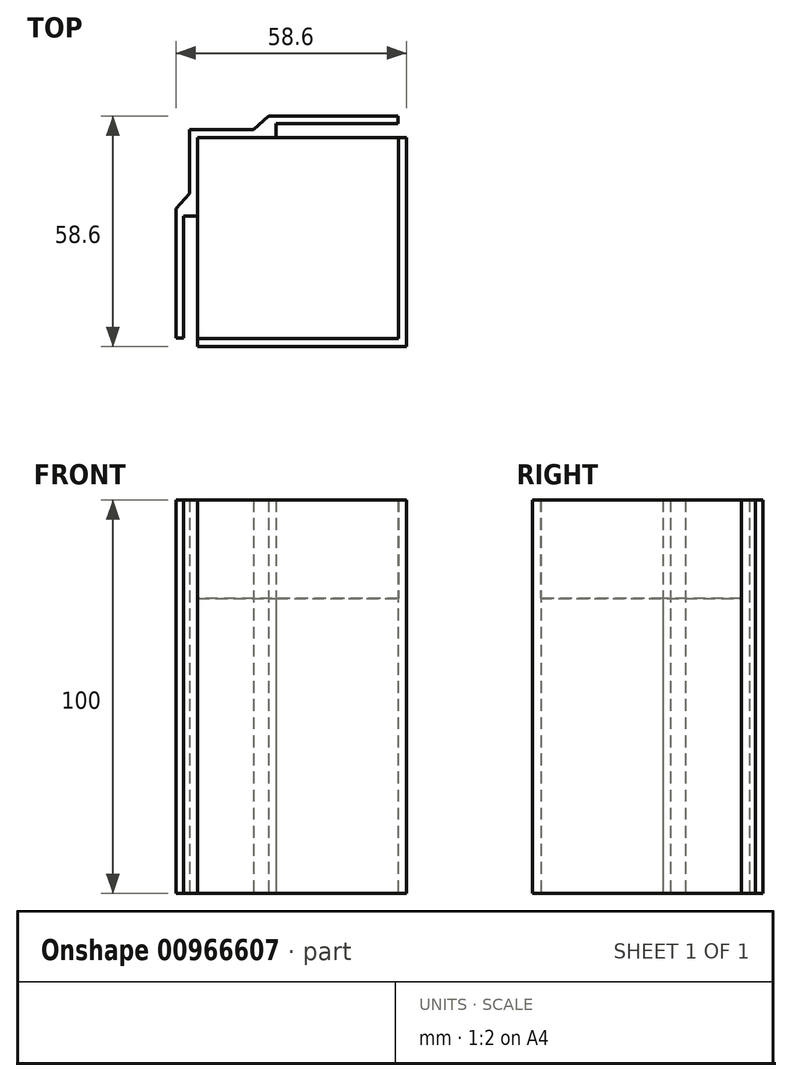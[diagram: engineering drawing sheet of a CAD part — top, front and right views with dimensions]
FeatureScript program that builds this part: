
annotation { "Feature Type Name" : "Feature", "Feature Type Description" : "" }
export const myFeature = defineFeature(function(context is Context, id is Id, definition is map)
    precondition{}
    {
        {
            var Q0;
            Q0=qCreatedBy(makeId("Top.planeOp"),FACE);
            var sketch = newSketch(context, id + "F0", { "sketchPlane" : qUnion([Q0])});
            skLineSegment(sketch, "E0.bottom", {"start": v(-25.5, 25.52) * mm, "end": v(25.5, 25.52) * mm});
            skLineSegment(sketch, "E0.top", {"start": v(-25.5, -25.48) * mm, "end": v(25.5, -25.48) * mm});
            skLineSegment(sketch, "E0.left", {"start": v(-25.5, 25.52) * mm, "end": v(-25.5, -25.48) * mm});
            skLineSegment(sketch, "E0.right", {"start": v(25.5, 25.52) * mm, "end": v(25.5, -25.48) * mm});
            skLineSegment(sketch, "E1", {"start": v(-25.5, 0.02) * mm, "end": v(25.5, 0.02) * mm});
            skLineSegment(sketch, "E2", {"start": v(0, 25.52) * mm, "end": v(0, -25.48) * mm});
            skLineSegment(sketch, "E3", {"start": v(-25.5, 25.52) * mm, "end": v(-25.5, 5.52) * mm});
            skLineSegment(sketch, "E4", {"start": v(-25.5, 5.52) * mm, "end": v(-29, 5.52) * mm});
            skLineSegment(sketch, "E5", {"start": v(-25.5, -25.48) * mm, "end": v(-29, -25.48) * mm});
            skLineSegment(sketch, "E6", {"start": v(-29, 5.52) * mm, "end": v(-29, -25.48) * mm});
            skLineSegment(sketch, "E7.0", {"start": v(-31, 7.52) * mm, "end": v(-31, -25.48) * mm});
            skLineSegment(sketch, "E7.1", {"start": v(-25.5, 7.52) * mm, "end": v(-31, 7.52) * mm});
            skLineSegment(sketch, "E8", {"start": v(-31, -25.48) * mm, "end": v(-29, -25.48) * mm});
            skLineSegment(sketch, "E9", {"start": v(-25.5, 25.52) * mm, "end": v(-5.5, 25.52) * mm});
            skLineSegment(sketch, "E10", {"start": v(-5.5, 25.52) * mm, "end": v(-5.5, 29.02) * mm});
            skLineSegment(sketch, "E11", {"start": v(25.5, 25.52) * mm, "end": v(25.5, 29.02) * mm});
            skLineSegment(sketch, "E12", {"start": v(-5.5, 29.02) * mm, "end": v(25.5, 29.02) * mm});
            skLineSegment(sketch, "E13.0", {"start": v(-7.5, 31.02) * mm, "end": v(25.5, 31.02) * mm});
            skLineSegment(sketch, "E13.1", {"start": v(-7.5, 25.52) * mm, "end": v(-7.5, 31.02) * mm});
            skLineSegment(sketch, "E14", {"start": v(25.5, 31.02) * mm, "end": v(25.5, 29.02) * mm});
            skLineSegment(sketch, "E15", {"start": v(-7.5, 25.52) * mm, "end": v(-7.56, 25.52) * mm});
            skLineSegment(sketch, "E16", {"start": v(-7.56, 25.52) * mm, "end": v(-7.5, 31.02) * mm});
            skLineSegment(sketch, "E17", {"start": v(-25.5, 7.52) * mm, "end": v(-25.5, 7.53) * mm});
            skLineSegment(sketch, "E18", {"start": v(-25.5, 7.53) * mm, "end": v(-31, 7.52) * mm});
            skLineSegment(sketch, "E19.0", {"start": v(-27.5, 27.52) * mm, "end": v(-0.5, 27.52) * mm});
            skLineSegment(sketch, "E19.1", {"start": v(-27.5, 27.52) * mm, "end": v(-27.5, 0.52) * mm});
            skLineSegment(sketch, "E20.0", {"start": v(-25.5, -25.58) * mm, "end": v(25.6, -25.58) * mm});
            skLineSegment(sketch, "E20.1", {"start": v(25.6, 25.52) * mm, "end": v(25.6, -25.58) * mm});
            skLineSegment(sketch, "E21.0", {"start": v(27.6, 25.52) * mm, "end": v(27.6, -27.58) * mm});
            skLineSegment(sketch, "E21.1", {"start": v(-25.5, -27.58) * mm, "end": v(27.6, -27.58) * mm});
            skLineSegment(sketch, "E22", {"start": v(-25.5, -25.48) * mm, "end": v(-25.5, -27.58) * mm});
            skLineSegment(sketch, "E23", {"start": v(27.6, 25.52) * mm, "end": v(25.5, 25.52) * mm});
            skLineSegment(sketch, "E24", {"start": v(-7.5, 31.02) * mm, "end": v(-13.36, 25.52) * mm});
            skLineSegment(sketch, "E25", {"start": v(-31, 7.52) * mm, "end": v(-25.5, 13.45) * mm});
            skSolve(sketch);
        }
        {
            var Q0;
            {var subQ0=sQuery(id+"F0.wireOp",EDGE,"E0.right");var subQ1=sQuery(id+"F0.wireOp",EDGE,"E0.top");var subQ2=makeQuery(id+"F0.imprint","INTERSECT",VERTEX,{"derivedFrom":[subQ1,subQ0]});Q0=makeQuery(id+"F0.imprint","IMPRINT",FACE,{"disambiguationData":[TD([[makeQuery(id+"F0.imprint","IMPRINT",EDGE,{"disambiguationData":[TD([[subQ2,1.0]])],"derivedFrom":subQ1}),1.0]])]});}
            var Q1;
            {var subQ6=sQuery(id+"F0.wireOp",EDGE,"E0.bottom");var subQ11=makeQuery(id+"F0.imprint","INTERSECT",VERTEX,{"derivedFrom":[subQ6,sQuery(id+"F0.wireOp",EDGE,"E24")]});Q1=makeQuery(id+"F0.imprint","IMPRINT",FACE,{"disambiguationData":[TD([[makeQuery(id+"F0.imprint","IMPRINT",EDGE,{"disambiguationData":[TD([[subQ11,1.0]])],"derivedFrom":subQ6}),-1.0]])]});}
            var Q2;
            {var subQ0=sQuery(id+"F0.wireOp",EDGE,"E7.1");var subQ1=sQuery(id+"F0.wireOp",EDGE,"E0.left");var subQ2=makeQuery(id+"F0.imprint","INTERSECT",VERTEX,{"derivedFrom":[subQ1,subQ0]});Q2=makeQuery(id+"F0.imprint","IMPRINT",FACE,{"disambiguationData":[TD([[makeQuery(id+"F0.imprint","IMPRINT",EDGE,{"disambiguationData":[TD([[subQ2,-1.0]])],"derivedFrom":subQ1}),-1.0]])]});}
            var Q3;
            {var subQ0=sQuery(id+"F0.wireOp",EDGE,"E13.1");var subQ1=sQuery(id+"F0.wireOp",EDGE,"E0.bottom");var subQ2=makeQuery(id+"F0.imprint","INTERSECT",VERTEX,{"derivedFrom":[subQ1,subQ0]});Q3=makeQuery(id+"F0.imprint","IMPRINT",FACE,{"disambiguationData":[TD([[makeQuery(id+"F0.imprint","IMPRINT",EDGE,{"disambiguationData":[TD([[subQ2,-1.0]])],"derivedFrom":subQ1}),1.0]])]});}
            var Q4;
            {var subQ3=sQuery(id+"F0.wireOp",EDGE,"E20.0");Q4=makeQuery(id+"F0.imprint","IMPRINT",FACE,{"disambiguationData":[TD([[makeQuery(id+"F0.imprint","IMPRINT",EDGE,{"derivedFrom":subQ3}),-1.0]])]});}
            var Q5;
            {var subQ1=sQuery(id+"F0.wireOp",EDGE,"E7.1");var subQ3=sQuery(id+"F0.wireOp",EDGE,"E19.1");var subQ4=makeQuery(id+"F0.imprint","INTERSECT",VERTEX,{"derivedFrom":[subQ1,subQ3]});Q5=makeQuery(id+"F0.imprint","IMPRINT",FACE,{"disambiguationData":[TD([[makeQuery(id+"F0.imprint","IMPRINT",EDGE,{"disambiguationData":[TD([[subQ4,1.0]])],"derivedFrom":subQ3}),-1.0]])]});}
            var Q6;
            {var subQ1=sQuery(id+"F0.wireOp",EDGE,"E13.1");var subQ3=sQuery(id+"F0.wireOp",EDGE,"E19.0");var subQ4=makeQuery(id+"F0.imprint","INTERSECT",VERTEX,{"derivedFrom":[subQ1,subQ3]});Q6=makeQuery(id+"F0.imprint","IMPRINT",FACE,{"disambiguationData":[TD([[makeQuery(id+"F0.imprint","IMPRINT",EDGE,{"disambiguationData":[TD([[subQ4,1.0]])],"derivedFrom":subQ3}),1.0]])]});}
            var Q7;
            {var subQ3=sQuery(id+"F0.wireOp",EDGE,"E24");var subQ9=sQuery(id+"F0.wireOp",EDGE,"E0.bottom");var subQ11=makeQuery(id+"F0.imprint","INTERSECT",VERTEX,{"derivedFrom":[subQ9,subQ3]});Q7=makeQuery(id+"F0.imprint","IMPRINT",FACE,{"disambiguationData":[TD([[makeQuery(id+"F0.imprint","IMPRINT",EDGE,{"disambiguationData":[TD([[subQ11,1.0]])],"derivedFrom":subQ9}),1.0]])]});}
            var Q8;
            {var subQ6=sQuery(id+"F0.wireOp",EDGE,"E6");Q8=makeQuery(id+"F0.imprint","IMPRINT",FACE,{"disambiguationData":[TD([[makeQuery(id+"F0.imprint","IMPRINT",EDGE,{"derivedFrom":subQ6}),-1.0]])]});}
            var Q9;
            {var subQ4=sQuery(id+"F0.wireOp",EDGE,"E12");Q9=makeQuery(id+"F0.imprint","IMPRINT",FACE,{"disambiguationData":[TD([[makeQuery(id+"F0.imprint","IMPRINT",EDGE,{"derivedFrom":subQ4}),1.0]])]});}
            var Q10;
            {var subQ0=sQuery(id+"F0.wireOp",EDGE,"E2");var subQ5=sQuery(id+"F0.wireOp",EDGE,"E1");var subQ7=makeQuery(id+"F0.imprint","INTERSECT",VERTEX,{"derivedFrom":[subQ5,subQ0]});Q10=makeQuery(id+"F0.imprint","IMPRINT",FACE,{"disambiguationData":[TD([[makeQuery(id+"F0.imprint","IMPRINT",EDGE,{"disambiguationData":[TD([[subQ7,-1.0]])],"derivedFrom":subQ5}),1.0]])]});}
            var Q11;
            {var subQ4=sQuery(id+"F0.wireOp",EDGE,"E20.0");Q11=makeQuery(id+"F0.imprint","IMPRINT",FACE,{"disambiguationData":[TD([[makeQuery(id+"F0.imprint","IMPRINT",EDGE,{"derivedFrom":subQ4}),1.0]])]});}
            var Q12;
            {var subQ0=sQuery(id+"F0.wireOp",EDGE,"E0.left");var subQ5=sQuery(id+"F0.wireOp",EDGE,"E1");var subQ6=makeQuery(id+"F0.imprint","INTERSECT",VERTEX,{"derivedFrom":[subQ0,subQ5]});Q12=makeQuery(id+"F0.imprint","IMPRINT",FACE,{"disambiguationData":[TD([[makeQuery(id+"F0.imprint","IMPRINT",EDGE,{"disambiguationData":[TD([[subQ6,-1.0]])],"derivedFrom":subQ5}),-1.0]])]});}
            var Q13;
            {var subQ0=sQuery(id+"F0.wireOp",EDGE,"E7.1");var subQ1=sQuery(id+"F0.wireOp",EDGE,"E0.left");var subQ2=makeQuery(id+"F0.imprint","INTERSECT",VERTEX,{"derivedFrom":[subQ1,subQ0]});Q13=makeQuery(id+"F0.imprint","IMPRINT",FACE,{"disambiguationData":[TD([[makeQuery(id+"F0.imprint","IMPRINT",EDGE,{"disambiguationData":[TD([[subQ2,1.0]])],"derivedFrom":subQ1}),-1.0]])]});}
            var Q14;
            {var subQ0=sQuery(id+"F0.wireOp",EDGE,"E13.1");var subQ1=sQuery(id+"F0.wireOp",EDGE,"E0.bottom");var subQ2=makeQuery(id+"F0.imprint","INTERSECT",VERTEX,{"derivedFrom":[subQ1,subQ0]});Q14=makeQuery(id+"F0.imprint","IMPRINT",FACE,{"disambiguationData":[TD([[makeQuery(id+"F0.imprint","IMPRINT",EDGE,{"disambiguationData":[TD([[subQ2,1.0]])],"derivedFrom":subQ1}),1.0]])]});}
            extrude(context, id + "F1", {"entities" : qUnion([Q0, Q1, Q2, Q3, Q4, Q5, Q6, Q7, Q8, Q9, Q10, Q11, Q12, Q13, Q14]), "depth" : 75 * mm, "offsetDistance" : 25 * mm});
        }
        {
            var Q0;
            {var subQ3=sQuery(id+"F0.wireOp",EDGE,"E24");var subQ9=sQuery(id+"F0.wireOp",EDGE,"E0.bottom");var subQ11=makeQuery(id+"F0.imprint","INTERSECT",VERTEX,{"derivedFrom":[subQ9,subQ3]});Q0=makeQuery(id+"F0.imprint","IMPRINT",FACE,{"disambiguationData":[TD([[makeQuery(id+"F0.imprint","IMPRINT",EDGE,{"disambiguationData":[TD([[subQ11,1.0]])],"derivedFrom":subQ9}),1.0]])]});}
            var Q1;
            {var subQ0=sQuery(id+"F0.wireOp",EDGE,"E13.1");var subQ1=sQuery(id+"F0.wireOp",EDGE,"E0.bottom");var subQ2=makeQuery(id+"F0.imprint","INTERSECT",VERTEX,{"derivedFrom":[subQ1,subQ0]});Q1=makeQuery(id+"F0.imprint","IMPRINT",FACE,{"disambiguationData":[TD([[makeQuery(id+"F0.imprint","IMPRINT",EDGE,{"disambiguationData":[TD([[subQ2,1.0]])],"derivedFrom":subQ1}),1.0]])]});}
            var Q2;
            {var subQ1=sQuery(id+"F0.wireOp",EDGE,"E13.1");var subQ3=sQuery(id+"F0.wireOp",EDGE,"E19.0");var subQ4=makeQuery(id+"F0.imprint","INTERSECT",VERTEX,{"derivedFrom":[subQ1,subQ3]});Q2=makeQuery(id+"F0.imprint","IMPRINT",FACE,{"disambiguationData":[TD([[makeQuery(id+"F0.imprint","IMPRINT",EDGE,{"disambiguationData":[TD([[subQ4,1.0]])],"derivedFrom":subQ3}),1.0]])]});}
            var Q3;
            {var subQ4=sQuery(id+"F0.wireOp",EDGE,"E12");Q3=makeQuery(id+"F0.imprint","IMPRINT",FACE,{"disambiguationData":[TD([[makeQuery(id+"F0.imprint","IMPRINT",EDGE,{"derivedFrom":subQ4}),1.0]])]});}
            var Q4;
            {var subQ0=sQuery(id+"F0.wireOp",EDGE,"E13.1");var subQ1=sQuery(id+"F0.wireOp",EDGE,"E0.bottom");var subQ2=makeQuery(id+"F0.imprint","INTERSECT",VERTEX,{"derivedFrom":[subQ1,subQ0]});Q4=makeQuery(id+"F0.imprint","IMPRINT",FACE,{"disambiguationData":[TD([[makeQuery(id+"F0.imprint","IMPRINT",EDGE,{"disambiguationData":[TD([[subQ2,-1.0]])],"derivedFrom":subQ1}),1.0]])]});}
            var Q5;
            {var subQ6=sQuery(id+"F0.wireOp",EDGE,"E6");Q5=makeQuery(id+"F0.imprint","IMPRINT",FACE,{"disambiguationData":[TD([[makeQuery(id+"F0.imprint","IMPRINT",EDGE,{"derivedFrom":subQ6}),-1.0]])]});}
            var Q6;
            {var subQ1=sQuery(id+"F0.wireOp",EDGE,"E7.1");var subQ3=sQuery(id+"F0.wireOp",EDGE,"E19.1");var subQ4=makeQuery(id+"F0.imprint","INTERSECT",VERTEX,{"derivedFrom":[subQ1,subQ3]});Q6=makeQuery(id+"F0.imprint","IMPRINT",FACE,{"disambiguationData":[TD([[makeQuery(id+"F0.imprint","IMPRINT",EDGE,{"disambiguationData":[TD([[subQ4,1.0]])],"derivedFrom":subQ3}),-1.0]])]});}
            var Q7;
            {var subQ0=sQuery(id+"F0.wireOp",EDGE,"E7.1");var subQ1=sQuery(id+"F0.wireOp",EDGE,"E0.left");var subQ2=makeQuery(id+"F0.imprint","INTERSECT",VERTEX,{"derivedFrom":[subQ1,subQ0]});Q7=makeQuery(id+"F0.imprint","IMPRINT",FACE,{"disambiguationData":[TD([[makeQuery(id+"F0.imprint","IMPRINT",EDGE,{"disambiguationData":[TD([[subQ2,1.0]])],"derivedFrom":subQ1}),-1.0]])]});}
            var Q8;
            {var subQ0=sQuery(id+"F0.wireOp",EDGE,"E7.1");var subQ1=sQuery(id+"F0.wireOp",EDGE,"E0.left");var subQ2=makeQuery(id+"F0.imprint","INTERSECT",VERTEX,{"derivedFrom":[subQ1,subQ0]});Q8=makeQuery(id+"F0.imprint","IMPRINT",FACE,{"disambiguationData":[TD([[makeQuery(id+"F0.imprint","IMPRINT",EDGE,{"disambiguationData":[TD([[subQ2,-1.0]])],"derivedFrom":subQ1}),-1.0]])]});}
            var Q9;
            {var subQ3=sQuery(id+"F0.wireOp",EDGE,"E20.0");Q9=makeQuery(id+"F0.imprint","IMPRINT",FACE,{"disambiguationData":[TD([[makeQuery(id+"F0.imprint","IMPRINT",EDGE,{"derivedFrom":subQ3}),-1.0]])]});}
            var Q10;
            {var subQ0=sQuery(id+"F0.wireOp",EDGE,"E25");var subQ1=sQuery(id+"F0.wireOp",EDGE,"E0.left");var subQ2=makeQuery(id+"F0.imprint","INTERSECT",VERTEX,{"derivedFrom":[subQ1,subQ0]});Q10=makeQuery(id+"F0.imprint","IMPRINT",FACE,{"disambiguationData":[TD([[makeQuery(id+"F0.imprint","IMPRINT",EDGE,{"disambiguationData":[TD([[subQ2,-1.0]])],"derivedFrom":subQ1}),-1.0]])]});}
            var Q11;
            {var subQ1=sQuery(id+"F0.wireOp",EDGE,"E18");var subQ3=sQuery(id+"F0.wireOp",EDGE,"E19.1");var subQ4=makeQuery(id+"F0.imprint","INTERSECT",VERTEX,{"derivedFrom":[subQ1,subQ3]});Q11=makeQuery(id+"F0.imprint","IMPRINT",FACE,{"disambiguationData":[TD([[makeQuery(id+"F0.imprint","IMPRINT",EDGE,{"disambiguationData":[TD([[subQ4,1.0]])],"derivedFrom":subQ3}),-1.0]])]});}
            var Q12;
            {var subQ1=sQuery(id+"F0.wireOp",EDGE,"E16");var subQ3=sQuery(id+"F0.wireOp",EDGE,"E19.0");var subQ4=makeQuery(id+"F0.imprint","INTERSECT",VERTEX,{"derivedFrom":[subQ1,subQ3]});Q12=makeQuery(id+"F0.imprint","IMPRINT",FACE,{"disambiguationData":[TD([[makeQuery(id+"F0.imprint","IMPRINT",EDGE,{"disambiguationData":[TD([[subQ4,1.0]])],"derivedFrom":subQ3}),1.0]])]});}
            var Q13;
            {var subQ0=sQuery(id+"F0.wireOp",EDGE,"E24");var subQ1=sQuery(id+"F0.wireOp",EDGE,"E0.bottom");var subQ2=makeQuery(id+"F0.imprint","INTERSECT",VERTEX,{"derivedFrom":[subQ1,subQ0]});Q13=makeQuery(id+"F0.imprint","IMPRINT",FACE,{"disambiguationData":[TD([[makeQuery(id+"F0.imprint","IMPRINT",EDGE,{"disambiguationData":[TD([[subQ2,-1.0]])],"derivedFrom":subQ1}),1.0]])]});}
            extrude(context, id + "F2", {"entities" : qUnion([Q0, Q1, Q2, Q3, Q4, Q5, Q6, Q7, Q8, Q9, Q10, Q11, Q12, Q13]), "operationType" : NewBodyOperationType.ADD, "depth" : 100 * mm, "offsetDistance" : 25 * mm});
        }
    });
